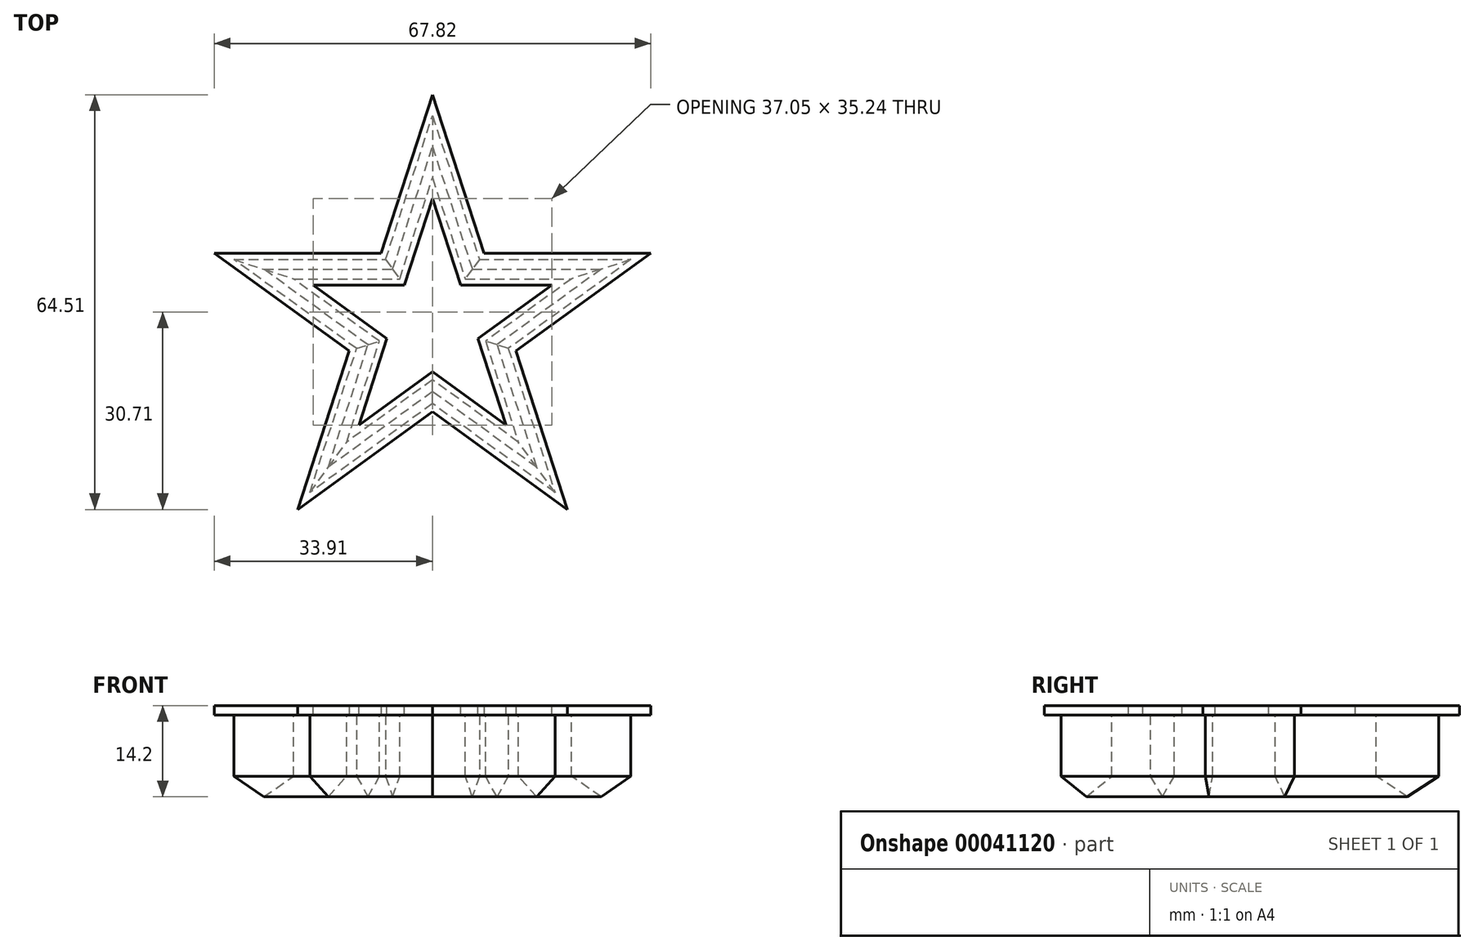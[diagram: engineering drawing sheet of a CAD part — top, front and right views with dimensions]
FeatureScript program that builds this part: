
annotation { "Feature Type Name" : "Feature", "Feature Type Description" : "" }
export const myFeature = defineFeature(function(context is Context, id is Id, definition is map)
    precondition{}
    {
        {
            var Q0;
            Q0=qCreatedBy(makeId("Top.planeOp"),FACE);
            var sketch = newSketch(context, id + "F0", { "sketchPlane" : qUnion([Q0])});
            skCircle(sketch, "E0.cCircle", {"center": v(0, 0) * mm, "radius": 27.57 * mm, "construction": true});
            skLineSegment(sketch, "E0.0", {"start": v(26.22, 8.52) * mm, "end": v(16.2, -22.3) * mm, "construction": true});
            skLineSegment(sketch, "E0.1", {"start": v(16.2, -22.3) * mm, "end": v(-16.2, -22.3) * mm, "construction": true});
            skLineSegment(sketch, "E0.2", {"start": v(-16.2, -22.3) * mm, "end": v(-26.22, 8.52) * mm, "construction": true});
            skLineSegment(sketch, "E0.3", {"start": v(-26.22, 8.52) * mm, "end": v(0, 27.57) * mm, "construction": true});
            skLineSegment(sketch, "E0.4", {"start": v(0, 27.57) * mm, "end": v(26.22, 8.52) * mm, "construction": true});
            skLineSegment(sketch, "E1", {"start": v(0, 27.57) * mm, "end": v(6.19, 8.52) * mm});
            skLineSegment(sketch, "E2", {"start": v(-26.22, 8.52) * mm, "end": v(-6.19, 8.52) * mm});
            skLineSegment(sketch, "E3", {"start": v(-16.2, -22.3) * mm, "end": v(-10.02, -3.25) * mm});
            skLineSegment(sketch, "E4", {"start": v(16.2, -22.3) * mm, "end": v(0, -10.53) * mm});
            skLineSegment(sketch, "E5", {"start": v(26.22, 8.52) * mm, "end": v(10.02, -3.25) * mm});
            skLineSegment(sketch, "E6.trimOffspring", {"start": v(-6.19, 8.52) * mm, "end": v(0, 27.57) * mm});
            skLineSegment(sketch, "E7.trimOffspring", {"start": v(6.19, 8.52) * mm, "end": v(26.22, 8.52) * mm});
            skLineSegment(sketch, "E8.trimOffspring", {"start": v(-10.02, -3.25) * mm, "end": v(-26.22, 8.52) * mm});
            skLineSegment(sketch, "E9.trimOffspring", {"start": v(0, -10.53) * mm, "end": v(-16.2, -22.3) * mm});
            skLineSegment(sketch, "E10.trimOffspring", {"start": v(10.02, -3.25) * mm, "end": v(16.2, -22.3) * mm});
            skCircle(sketch, "E11", {"center": v(63.21, 1.28) * mm, "radius": 7.5 * mm});
            skSolve(sketch);
        }
        {
            var Q0;
            Q0=qCreatedBy(makeId("Right.planeOp"),FACE);
            var Q1;
            Q1=sQuery(id+"F0.wireOp",VERTEX,"E1.end");
            cPlane(context, id + "F1", {"entities" : qUnion([Q0, Q1]), "cplaneType" : CPlaneType.PLANE_POINT, "offset" : 150 * mm, "width" : 150 * mm, "height" : 150 * mm});
        }
        {
            var Q0;
            Q0=qCreatedBy(id+"F1.planeOp",FACE);
            var sketch = newSketch(context, id + "F2", { "sketchPlane" : qUnion([Q0])});
            skPoint(sketch, "E12.0", {"position": v(8.52, 0) * mm});
            skLineSegment(sketch, "E13", {"start": v(8.52, 0) * mm, "end": v(10.02, 3.22) * mm});
            skLineSegment(sketch, "E14", {"start": v(10.02, 3.22) * mm, "end": v(10.02, 12.7) * mm});
            skLineSegment(sketch, "E15", {"start": v(10.02, 12.7) * mm, "end": v(11.02, 12.7) * mm});
            skLineSegment(sketch, "E16", {"start": v(11.02, 12.7) * mm, "end": v(11.02, 14.2) * mm});
            skLineSegment(sketch, "E17", {"start": v(11.02, 14.2) * mm, "end": v(8.52, 14.2) * mm});
            skLineSegment(sketch, "E18", {"start": v(8.52, 14.2) * mm, "end": v(8.52, 0) * mm, "construction": true});
            skLineSegment(sketch, "E19.MirrorCS", {"start": v(7.02, 12.7) * mm, "end": v(6.02, 12.7) * mm});
            skLineSegment(sketch, "E20.MirrorCS", {"start": v(6.02, 12.7) * mm, "end": v(6.02, 14.2) * mm});
            skLineSegment(sketch, "E21.MirrorCS", {"start": v(7.02, 3.22) * mm, "end": v(7.02, 12.7) * mm});
            skLineSegment(sketch, "E22.MirrorCS", {"start": v(6.02, 14.2) * mm, "end": v(8.52, 14.2) * mm});
            skLineSegment(sketch, "E23.MirrorCS", {"start": v(8.52, 0) * mm, "end": v(7.02, 3.22) * mm});
            skSolve(sketch);
        }
        {
            var Q0;
            Q0 = qSketchRegion(id + "F2", true);
            var Q1;
            Q1=sQuery(id+"F0.wireOp",EDGE,"E7.trimOffspring");
            var Q2;
            Q2=sQuery(id+"F0.wireOp",EDGE,"E5");
            var Q3;
            Q3=sQuery(id+"F0.wireOp",EDGE,"E10.trimOffspring");
            var Q4;
            Q4=sQuery(id+"F0.wireOp",EDGE,"E4");
            var Q5;
            Q5=sQuery(id+"F0.wireOp",EDGE,"E9.trimOffspring");
            var Q6;
            Q6=sQuery(id+"F0.wireOp",EDGE,"E3");
            var Q7;
            Q7=sQuery(id+"F0.wireOp",EDGE,"E8.trimOffspring");
            var Q8;
            Q8=sQuery(id+"F0.wireOp",EDGE,"E2");
            var Q9;
            Q9=sQuery(id+"F0.wireOp",EDGE,"E6.trimOffspring");
            var Q10;
            Q10=sQuery(id+"F0.wireOp",EDGE,"E1");
            sweep(context, id + "F3", {"profiles" : qUnion([Q0]), "path" : qUnion([Q1, Q2, Q3, Q4, Q5, Q6, Q7, Q8, Q9, Q10])});
        }
    });
